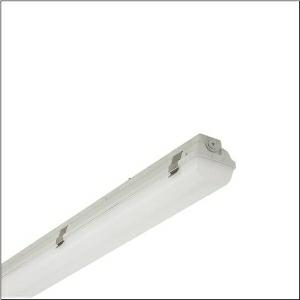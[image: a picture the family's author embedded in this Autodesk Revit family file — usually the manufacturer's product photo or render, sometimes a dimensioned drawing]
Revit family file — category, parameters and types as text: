
# Revit family: monsun_r__21_eco_51fj20dl45a_bcca
name_source: partatom
category: Lighting Fixtures
units: mm (PartAtom-declared; Revit-internal decimal feet)

## family parameters
Cut with Voids When Loaded = No
Host = Face
Light Source = No
Part Type = Normal
Room Calculation Point = No
Round Connector Dimension = Use Diameter
Shared = No

## types (1)
- Monsun® 21 Eco (1 x LED, 4900 lm, 36 W, 4000K)
    Apparent Load = 36 VA
    CIE Flux Codes = 40 69 88 88 100
    Color Rendering = 80
    Color Temperature = 4000K
    Default Elevation = 1800 mm
    Description = Monsun® 21 Eco, damp-proof luminaire, primary optical cover: diffuser, of PC, UV-stabilised, frosted, light emission: direct distribution, primary light characteristic: symmetric, installation type: suspended mounting, surface-mounted, LED, rated luminous flux: 4.900lm, luminous efficacy: 132lm/W, light colour: 840, colour temperature: 4000K, control gear: ECG DALI, with terminal, 5-pole, max. 2.5mm², mains connection: 220..240V, AC, 50/60Hz, rated input power: 36W, housing, of glass-fibre reinforced polyester, light grey (RAL 7035), length: 1.277mm, width: 90mm, height: 95mm, clip for enclosure, of spring steel V2A, protection rating (complete): IP66, insulation class (complete): insulation class I (protective earthing), certification: CE, UKCA, protection symbol: D, impact resistance: IK08, permissible operating ambient temperature: -20..+35°C, corresponds to IFS (International Featured Standards) requirements for safety and quality in the food industry, packaging unit: 1 piece
    Height = 103 mm
    Lamp = 1 x LED
    Lamp Light Flux = 4900 lm
    Lamp Power = 36 W
    Lamp count = 1
    Length = 1277 mm
    Luminous efficacy = 136 lm/W
    Manufacturer = Siteco
    ModVariant = No
    Model = 51FJ20DL45A
    Mounting Place = Ceiling
    Mounting Type = Surface mounted
    Number of Poles = 1
    OnlyDefault = Yes
    Power Factor = 1
    Product Name = Monsun® 21 Eco
    Product group = damp-proof luminaire | ceiling mounted
    ProductGroupID = 300
    Protection Class = Protection class I
    Protection Degree = IP 66
    RLX_Detail_Level = 1
    RlxData = <blob elided: 33177 chars, md5=20a61fc7>
    Socket = socket
    Standby Power = 0 W
    System Light Flux = 4900 lm
    System Power = 36 W
    Type Comments = Product without accessories
    Type Image = l_1007218.jpg
    URL = http://relux.com
    VarID = ---
    Voltage = 0 V
    Weight = 0.00 kg
    Width = 90 mm

## geometry (parser evidence)
native form markers: Blend x4, Sweep x11
no freeform markers — native parametric forms only
